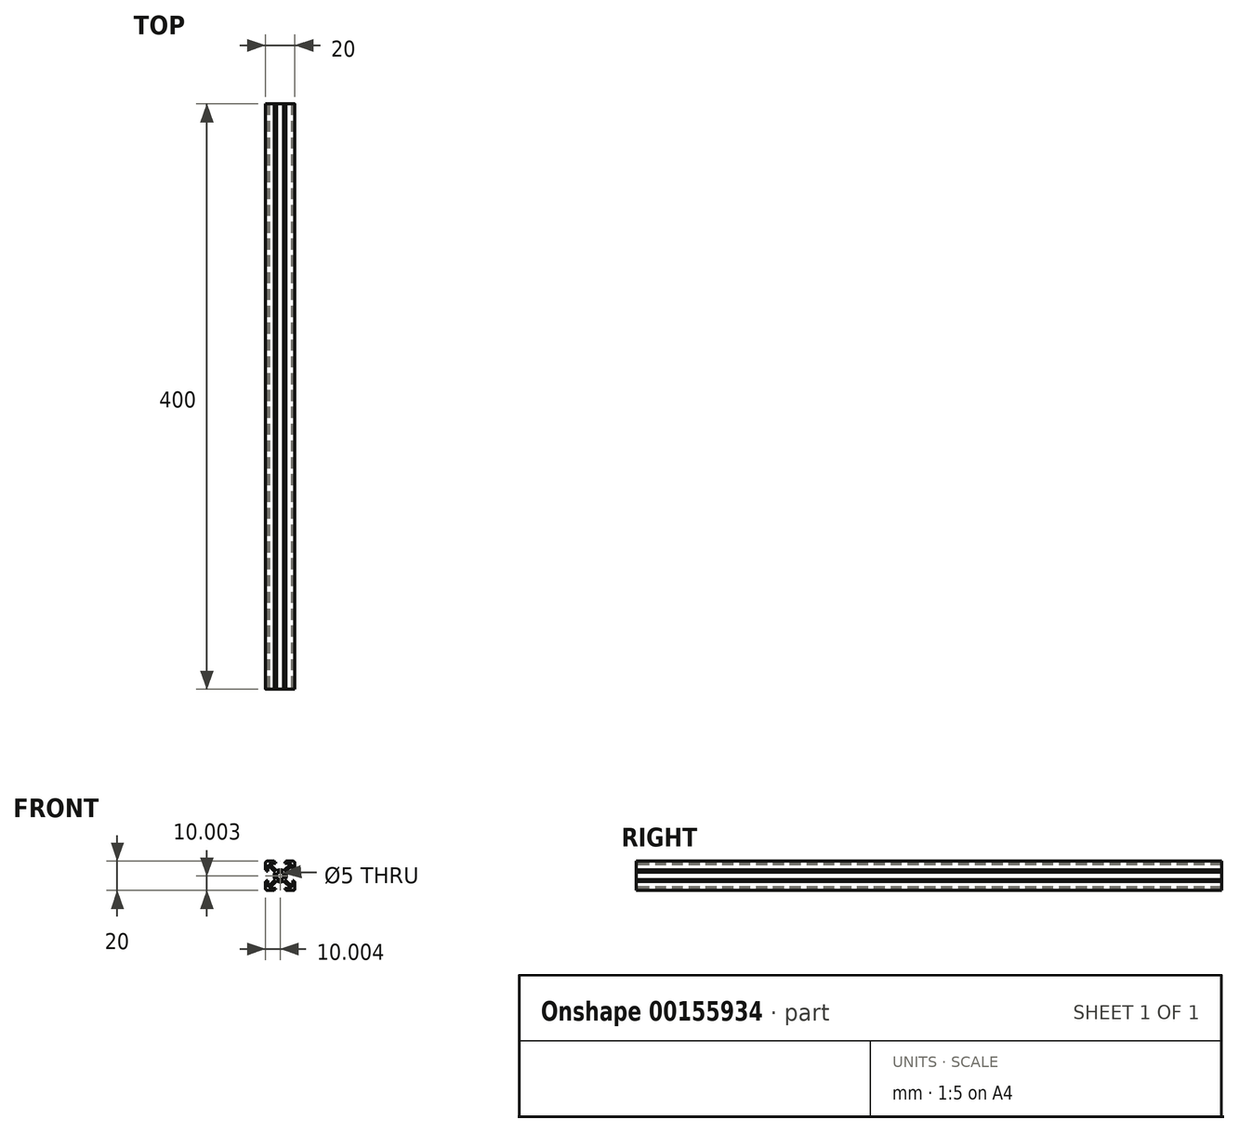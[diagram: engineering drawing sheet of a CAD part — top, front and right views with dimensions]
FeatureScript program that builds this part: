
annotation { "Feature Type Name" : "Feature", "Feature Type Description" : "" }
export const myFeature = defineFeature(function(context is Context, id is Id, definition is map)
    precondition{}
    {
        {
            var Q0;
            Q0=qCreatedBy(makeId("Front.planeOp"),FACE);
            var sketch = newSketch(context, id + "F0", { "sketchPlane" : qUnion([Q0])});
            skArc(sketch, "E0", {"start": v(-44.98, 42.64) * mm, "mid": v(-45.76, 40.2) * mm, "end": v(-44.98, 37.77) * mm});
            skCircle(sketch, "E1", {"center": v(-41.56, 40.2) * mm, "radius": 2.5 * mm});
            skLineSegment(sketch, "E2", {"start": v(-54.61, 53.26) * mm, "end": v(-41.56, 40.2) * mm, "construction": true});
            skLineSegment(sketch, "E3", {"start": v(-41.56, 40.2) * mm, "end": v(-28.67, 27.32) * mm, "construction": true});
            skLineSegment(sketch, "E4", {"start": v(-41.56, 40.2) * mm, "end": v(-29.82, 51.94) * mm, "construction": true});
            skLineSegment(sketch, "E5", {"start": v(-41.56, 40.2) * mm, "end": v(-53.14, 28.61) * mm, "construction": true});
            skLineSegment(sketch, "E6", {"start": v(-55.54, 40.2) * mm, "end": v(-21.72, 40.2) * mm, "construction": true});
            skLineSegment(sketch, "E7", {"start": v(-41.56, 50.17) * mm, "end": v(-41.56, 24.27) * mm, "construction": true});
            skLineSegment(sketch, "E8", {"start": v(-50.36, 50.2) * mm, "end": v(-45.5, 50.2) * mm});
            skLineSegment(sketch, "E9", {"start": v(-44.76, 49.6) * mm, "end": v(-44.76, 48.8) * mm});
            skLineSegment(sketch, "E10", {"start": v(-49.17, 48.8) * mm, "end": v(-43.99, 43.63) * mm});
            skLineSegment(sketch, "E11", {"start": v(-44.76, 48.8) * mm, "end": v(-49.17, 48.8) * mm});
            skLineSegment(sketch, "E12", {"start": v(-45.5, 50.2) * mm, "end": v(-45.5, 49.6) * mm});
            skLineSegment(sketch, "E13", {"start": v(-45.5, 49.6) * mm, "end": v(-44.76, 49.6) * mm});
            skPoint(sketch, "E14.orphan", {"position": v(-44.76, 50.2) * mm});
            skLineSegment(sketch, "E15.MirrorCS", {"start": v(-50.16, 47.81) * mm, "end": v(-44.98, 42.64) * mm});
            skLineSegment(sketch, "E16.MirrorCS", {"start": v(-50.16, 43.4) * mm, "end": v(-50.16, 47.81) * mm});
            skLineSegment(sketch, "E17.MirrorCS", {"start": v(-50.95, 43.4) * mm, "end": v(-50.16, 43.4) * mm});
            skLineSegment(sketch, "E18.MirrorCS", {"start": v(-50.95, 44.15) * mm, "end": v(-50.95, 43.4) * mm});
            skLineSegment(sketch, "E19.MirrorCS", {"start": v(-51.56, 49) * mm, "end": v(-51.56, 44.15) * mm});
            skLineSegment(sketch, "E20.MirrorCS", {"start": v(-51.56, 44.15) * mm, "end": v(-50.95, 44.15) * mm});
            skLineSegment(sketch, "E21.MirrorCS", {"start": v(-32.96, 47.81) * mm, "end": v(-38.13, 42.64) * mm});
            skLineSegment(sketch, "E22.MirrorCS", {"start": v(-33.95, 48.8) * mm, "end": v(-39.12, 43.63) * mm});
            skLineSegment(sketch, "E23.MirrorCS", {"start": v(-37.6, 49.6) * mm, "end": v(-38.36, 49.6) * mm});
            skLineSegment(sketch, "E24.MirrorCS", {"start": v(-32.16, 44.15) * mm, "end": v(-32.16, 43.4) * mm});
            skLineSegment(sketch, "E25.MirrorCS", {"start": v(-31.56, 44.15) * mm, "end": v(-32.16, 44.15) * mm});
            skLineSegment(sketch, "E26.MirrorCS", {"start": v(-38.36, 49.6) * mm, "end": v(-38.36, 48.8) * mm});
            skLineSegment(sketch, "E27.MirrorCS", {"start": v(-37.6, 50.2) * mm, "end": v(-37.6, 49.6) * mm});
            skLineSegment(sketch, "E28.MirrorCS", {"start": v(-32.16, 43.4) * mm, "end": v(-32.96, 43.4) * mm});
            skLineSegment(sketch, "E29.MirrorCS", {"start": v(-32.96, 43.4) * mm, "end": v(-32.96, 47.81) * mm});
            skPoint(sketch, "E30.MirrorP", {"position": v(-38.36, 50.2) * mm});
            skLineSegment(sketch, "E31.MirrorCS", {"start": v(-38.36, 48.8) * mm, "end": v(-33.95, 48.8) * mm});
            skLineSegment(sketch, "E32.MirrorCS", {"start": v(-32.76, 50.2) * mm, "end": v(-37.6, 50.2) * mm});
            skLineSegment(sketch, "E33.MirrorCS", {"start": v(-31.56, 49) * mm, "end": v(-31.56, 44.15) * mm});
            skLineSegment(sketch, "E34.MirrorCS", {"start": v(-32.16, 37) * mm, "end": v(-32.96, 37) * mm});
            skLineSegment(sketch, "E35.MirrorCS", {"start": v(-38.36, 30.8) * mm, "end": v(-38.36, 31.6) * mm});
            skLineSegment(sketch, "E36.MirrorCS", {"start": v(-32.16, 36.25) * mm, "end": v(-32.16, 37) * mm});
            skLineSegment(sketch, "E37.MirrorCS", {"start": v(-37.6, 30.8) * mm, "end": v(-38.36, 30.8) * mm});
            skLineSegment(sketch, "E38.MirrorCS", {"start": v(-31.56, 36.25) * mm, "end": v(-32.16, 36.25) * mm});
            skLineSegment(sketch, "E39.MirrorCS", {"start": v(-37.6, 30.2) * mm, "end": v(-37.6, 30.8) * mm});
            skLineSegment(sketch, "E40.MirrorCS", {"start": v(-32.76, 30.2) * mm, "end": v(-37.6, 30.2) * mm});
            skLineSegment(sketch, "E41.MirrorCS", {"start": v(-31.56, 31.4) * mm, "end": v(-31.56, 36.25) * mm});
            skLineSegment(sketch, "E42.MirrorCS", {"start": v(-33.95, 31.6) * mm, "end": v(-39.12, 36.78) * mm});
            skLineSegment(sketch, "E43.MirrorCS", {"start": v(-32.96, 37) * mm, "end": v(-32.96, 32.6) * mm});
            skPoint(sketch, "E44.MirrorP", {"position": v(-38.36, 30.2) * mm});
            skLineSegment(sketch, "E45.MirrorCS", {"start": v(-38.36, 31.6) * mm, "end": v(-33.95, 31.6) * mm});
            skLineSegment(sketch, "E46.MirrorCS", {"start": v(-32.96, 32.6) * mm, "end": v(-38.13, 37.77) * mm});
            skLineSegment(sketch, "E47.MirrorCS", {"start": v(-45.5, 30.8) * mm, "end": v(-44.76, 30.8) * mm});
            skLineSegment(sketch, "E48.MirrorCS", {"start": v(-51.56, 36.25) * mm, "end": v(-50.95, 36.25) * mm});
            skLineSegment(sketch, "E49.MirrorCS", {"start": v(-50.95, 36.25) * mm, "end": v(-50.95, 37) * mm});
            skLineSegment(sketch, "E50.MirrorCS", {"start": v(-50.95, 37) * mm, "end": v(-50.16, 37) * mm});
            skLineSegment(sketch, "E51.MirrorCS", {"start": v(-45.5, 30.2) * mm, "end": v(-45.5, 30.8) * mm});
            skLineSegment(sketch, "E52.MirrorCS", {"start": v(-44.76, 30.8) * mm, "end": v(-44.76, 31.6) * mm});
            skLineSegment(sketch, "E53.MirrorCS", {"start": v(-50.16, 37) * mm, "end": v(-50.16, 32.6) * mm});
            skLineSegment(sketch, "E54.MirrorCS", {"start": v(-50.16, 32.6) * mm, "end": v(-44.98, 37.77) * mm});
            skLineSegment(sketch, "E55.MirrorCS", {"start": v(-50.36, 30.2) * mm, "end": v(-45.5, 30.2) * mm});
            skPoint(sketch, "E56.MirrorP", {"position": v(-44.76, 30.2) * mm});
            skLineSegment(sketch, "E57.MirrorCS", {"start": v(-51.56, 31.4) * mm, "end": v(-51.56, 36.25) * mm});
            skLineSegment(sketch, "E58.MirrorCS", {"start": v(-49.17, 31.6) * mm, "end": v(-43.99, 36.78) * mm});
            skLineSegment(sketch, "E59.MirrorCS", {"start": v(-44.76, 31.6) * mm, "end": v(-49.17, 31.6) * mm});
            skPoint(sketch, "E60.visualSharp", {"position": v(-51.56, 50.2) * mm});
            skArc(sketch, "E60.filletArc", {"start": v(-50.36, 50.2) * mm, "mid": v(-51.2, 49.85) * mm, "end": v(-51.56, 49) * mm});
            skPoint(sketch, "E61.visualSharp", {"position": v(-31.56, 50.2) * mm});
            skArc(sketch, "E61.filletArc", {"start": v(-31.56, 49) * mm, "mid": v(-31.9, 49.85) * mm, "end": v(-32.76, 50.2) * mm});
            skPoint(sketch, "E62.visualSharp", {"position": v(-31.56, 30.2) * mm});
            skArc(sketch, "E62.filletArc", {"start": v(-32.76, 30.2) * mm, "mid": v(-31.9, 30.55) * mm, "end": v(-31.56, 31.4) * mm});
            skPoint(sketch, "E63.visualSharp", {"position": v(-51.56, 30.2) * mm});
            skArc(sketch, "E63.filletArc", {"start": v(-51.56, 31.4) * mm, "mid": v(-51.2, 30.55) * mm, "end": v(-50.36, 30.2) * mm});
            skArc(sketch, "E64.trimOffspring", {"start": v(-39.12, 43.63) * mm, "mid": v(-41.56, 44.4) * mm, "end": v(-43.99, 43.63) * mm});
            skArc(sketch, "E65.trimOffspring", {"start": v(-43.99, 36.78) * mm, "mid": v(-41.56, 36) * mm, "end": v(-39.12, 36.78) * mm});
            skArc(sketch, "E66.trimOffspring", {"start": v(-38.13, 37.77) * mm, "mid": v(-37.36, 40.2) * mm, "end": v(-38.13, 42.64) * mm});
            skSolve(sketch);
        }
        {
            var Q0;
            Q0=makeQuery(id+"F0.imprint","IMPRINT",FACE,{"disambiguationData":[TD([[makeQuery(id+"F0.imprint","IMPRINT",EDGE,{"derivedFrom":sQuery(id+"F0.wireOp",EDGE,"E0")}),1.0]])]});
            extrude(context, id + "F1", {"entities" : qUnion([Q0]), "oppositeDirection" : true, "depth" : 400 * mm});
        }
    });
